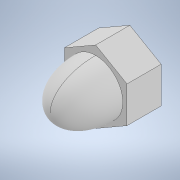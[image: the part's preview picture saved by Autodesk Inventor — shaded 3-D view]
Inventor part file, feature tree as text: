
AUTODESK INVENTOR PART (.ipt)
format: ipt  version: 2022 (Build 260153000, 153)  size: 173,568 bytes
history: native  units: mm
features: sketch x2, extrude x1, revolve x1, thread x1
ambient origin geometry x8: Origin, YZ Plane, XZ Plane, XY Plane, X Axis, Y Axis, Z Axis, Center Point
bodies: Solid1 (feature_tree)
feature tree (5):
  extrude  "Extrusion1"  Depth=3.0mm
  revolve  "Revolution1"  [1 undecoded]
  thread  "Thread1"  [1 undecoded]
  sketch  "Sketch1"  dims[d0=5.5mm d1=3.0mm]
  sketch  "Sketch2"  dims[d2=3.0mm d3=0.0mm d4=7.0mm d5=90.0deg d6=3.0mm d7=0.0mm]
note: 2 required parameter values undecoded (feature->parameter linkage not recoverable at this tier; creation-order binding heuristic only, values carry confidence <= 0.55)